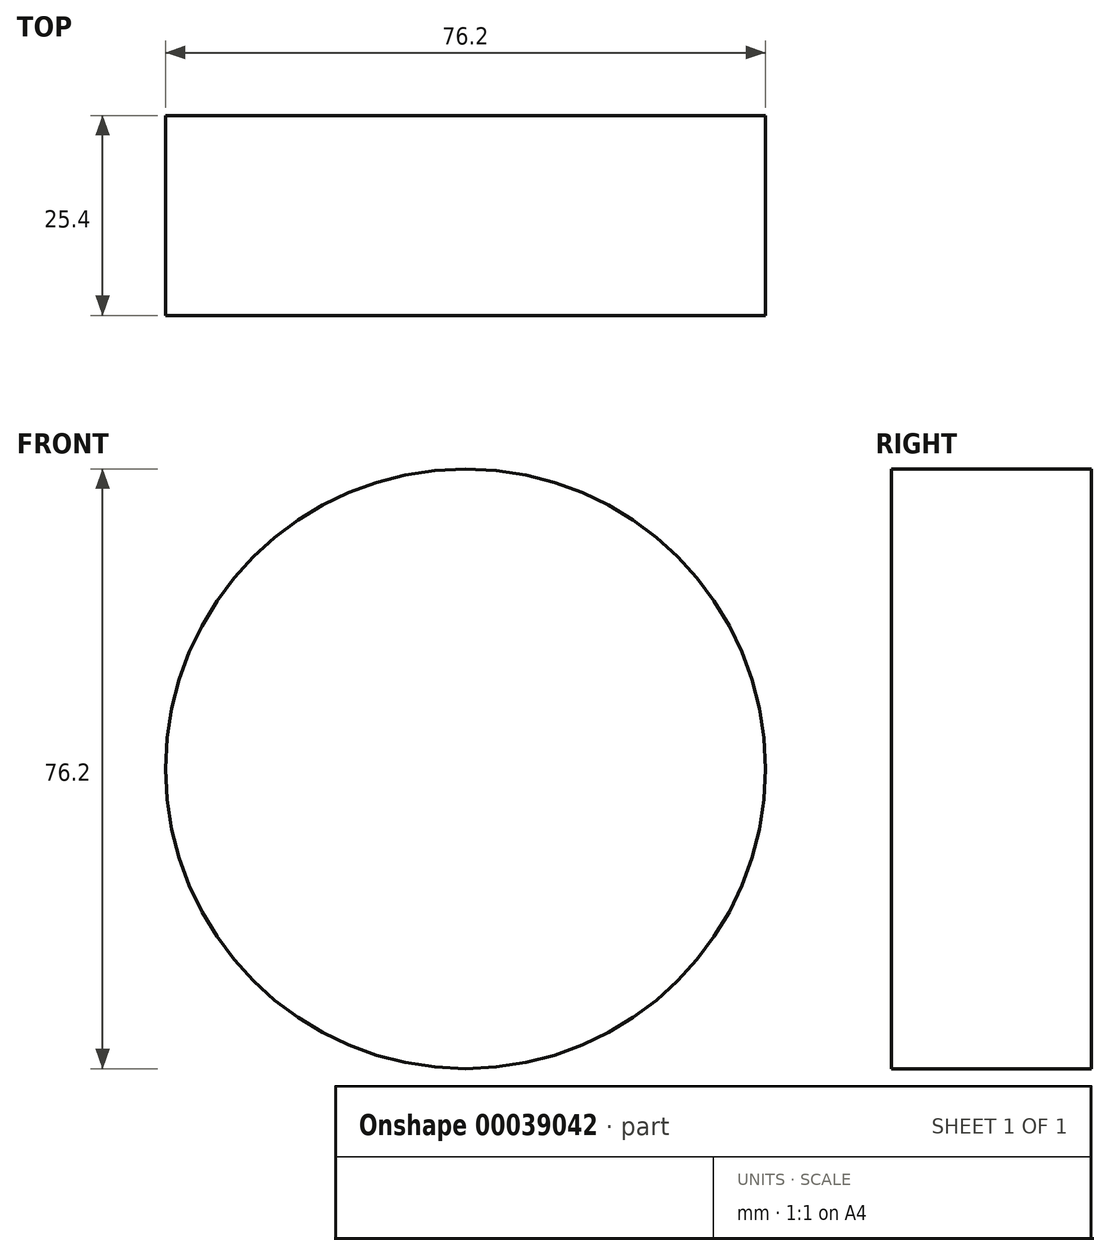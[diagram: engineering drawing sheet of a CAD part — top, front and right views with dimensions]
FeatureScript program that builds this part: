
annotation { "Feature Type Name" : "Feature", "Feature Type Description" : "" }
export const myFeature = defineFeature(function(context is Context, id is Id, definition is map)
    precondition{}
    {
        {
            var Q0;
            Q0=qCreatedBy(makeId("Front.planeOp"),FACE);
            var sketch = newSketch(context, id + "F0", { "sketchPlane" : qUnion([Q0])});
            skCircle(sketch, "E0", {"center": v(0, 0) * mm, "radius": 38.1 * mm});
            skSolve(sketch);
        }
        {
            var Q0;
            Q0 = qSketchRegion(id + "F0", true);
            var Q1;
            Q1=makeQuery(id+"F0.imprint","IMPRINT",FACE,{"disambiguationData":[TD([[makeQuery(id+"F0.imprint","IMPRINT",EDGE,{"derivedFrom":sQuery(id+"F0.wireOp",EDGE,"E0")}),1.0]])]});
            var Q2;
            Q2=sQuery(id+"F0.wireOp",EDGE,"E0");
            extrude(context, id + "F1", {"entities" : qUnion([Q0, Q1]), "bodyType" : ToolBodyType.SURFACE, "surfaceEntities" : qUnion([Q2]), "depth" : 25.4 * mm});
        }
    });
